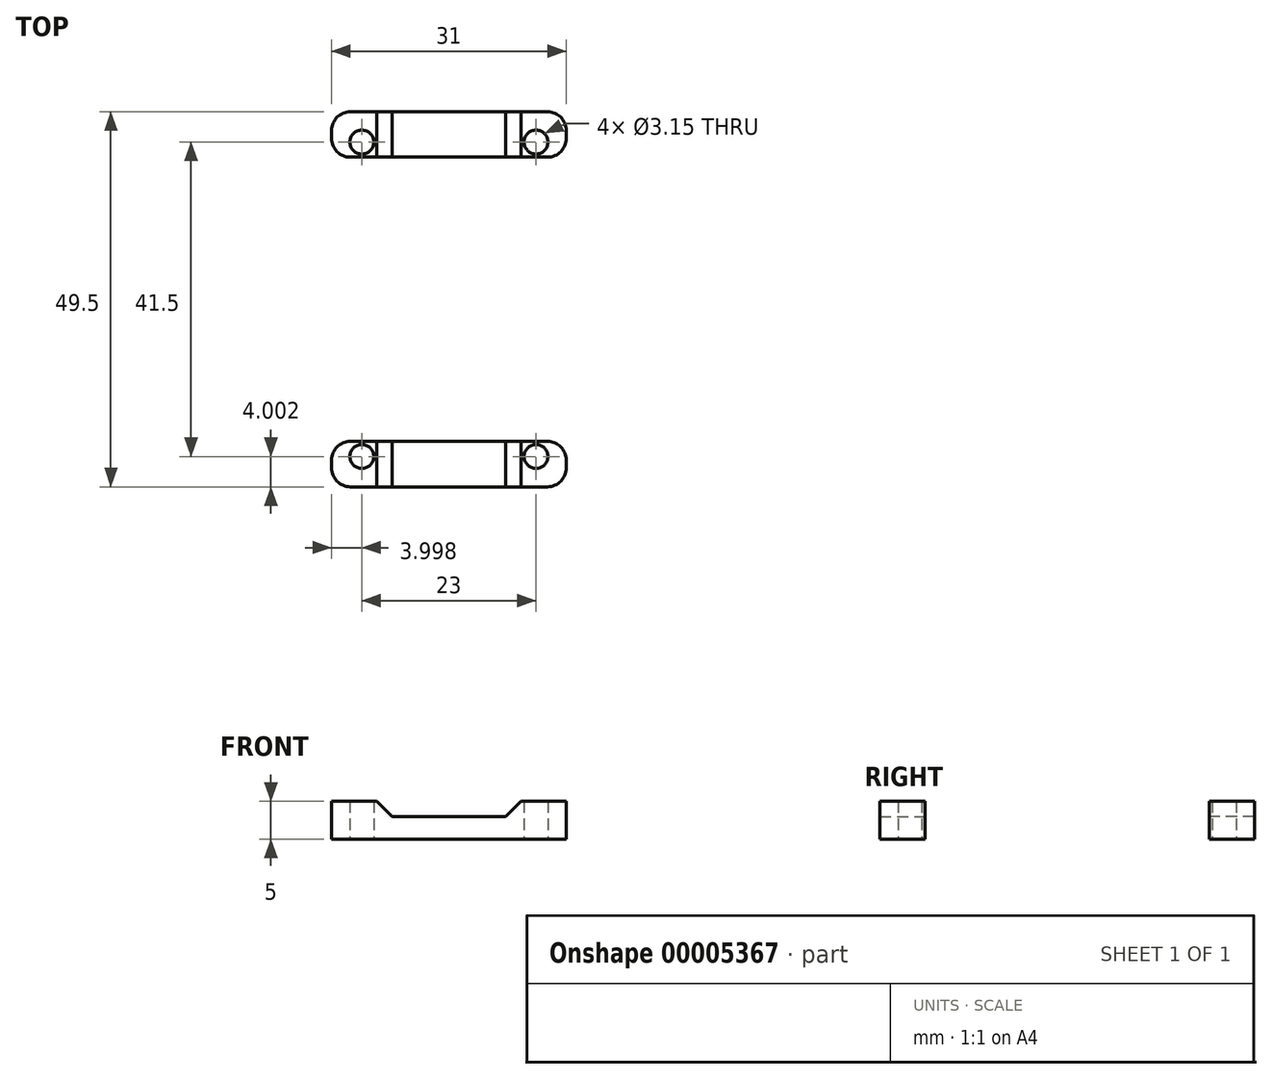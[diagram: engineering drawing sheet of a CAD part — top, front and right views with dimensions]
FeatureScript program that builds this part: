
annotation { "Feature Type Name" : "Feature", "Feature Type Description" : "" }
export const myFeature = defineFeature(function(context is Context, id is Id, definition is map)
    precondition{}
    {
        {
            var Q0;
            Q0=qCreatedBy(makeId("Top.planeOp"),FACE);
            var sketch = newSketch(context, id + "F0", { "sketchPlane" : qUnion([Q0])});
            skCircle(sketch, "E0", {"center": v(-6.84, -9.47) * mm, "radius": 1.57 * mm});
            skCircle(sketch, "E1", {"center": v(16.16, -9.47) * mm, "radius": 1.57 * mm});
            skCircle(sketch, "E2", {"center": v(16.16, 32.03) * mm, "radius": 1.57 * mm});
            skCircle(sketch, "E3", {"center": v(-6.84, 32.03) * mm, "radius": 1.57 * mm});
            skLineSegment(sketch, "E4.bottom", {"start": v(-10.84, 36.03) * mm, "end": v(20.16, 36.03) * mm});
            skLineSegment(sketch, "E4.top", {"start": v(-10.84, -13.47) * mm, "end": v(20.16, -13.47) * mm});
            skLineSegment(sketch, "E4.left", {"start": v(-10.84, 36.03) * mm, "end": v(-10.84, -13.47) * mm});
            skLineSegment(sketch, "E4.right", {"start": v(20.16, 36.03) * mm, "end": v(20.16, -13.47) * mm});
            skLineSegment(sketch, "E5", {"start": v(-4.84, 36.03) * mm, "end": v(-4.84, -13.47) * mm});
            skLineSegment(sketch, "E6", {"start": v(14.16, 36.03) * mm, "end": v(14.16, -13.47) * mm});
            skLineSegment(sketch, "E7", {"start": v(-10.84, 30.03) * mm, "end": v(20.16, 30.03) * mm});
            skLineSegment(sketch, "E8", {"start": v(-10.84, -7.47) * mm, "end": v(20.16, -7.47) * mm});
            skSolve(sketch);
        }
        {
            var Q0;
            Q0=makeQuery(id+"F0.imprint","IMPRINT",FACE,{"disambiguationData":[TD([[makeQuery(id+"F0.imprint","IMPRINT",EDGE,{"derivedFrom":sQuery(id+"F0.wireOp",EDGE,"E0")}),-1.0]])]});
            var Q1;
            Q1=makeQuery(id+"F0.imprint","IMPRINT",FACE,{"disambiguationData":[TD([[makeQuery(id+"F0.imprint","IMPRINT",EDGE,{"derivedFrom":sQuery(id+"F0.wireOp",EDGE,"E1")}),-1.0]])]});
            var Q2;
            Q2=makeQuery(id+"F0.imprint","IMPRINT",FACE,{"disambiguationData":[TD([[makeQuery(id+"F0.imprint","IMPRINT",EDGE,{"derivedFrom":sQuery(id+"F0.wireOp",EDGE,"E2")}),-1.0]])]});
            var Q3;
            Q3=makeQuery(id+"F0.imprint","IMPRINT",FACE,{"disambiguationData":[TD([[makeQuery(id+"F0.imprint","IMPRINT",EDGE,{"derivedFrom":sQuery(id+"F0.wireOp",EDGE,"E3")}),-1.0]])]});
            var Q4;
            {var subQ3=sQuery(id+"F0.wireOp",EDGE,"E5");var subQ5=sQuery(id+"F0.wireOp",EDGE,"E4.bottom");var subQ6=makeQuery(id+"F0.imprint","INTERSECT",VERTEX,{"derivedFrom":[subQ5,subQ3]});Q4=makeQuery(id+"F0.imprint","IMPRINT",FACE,{"disambiguationData":[TD([[makeQuery(id+"F0.imprint","IMPRINT",EDGE,{"disambiguationData":[TD([[subQ6,-1.0]])],"derivedFrom":subQ5}),-1.0]])]});}
            var Q5;
            {var subQ3=sQuery(id+"F0.wireOp",EDGE,"E4.top");var subQ5=sQuery(id+"F0.wireOp",EDGE,"E5");var subQ7=makeQuery(id+"F0.imprint","INTERSECT",VERTEX,{"derivedFrom":[subQ3,subQ5]});Q5=makeQuery(id+"F0.imprint","IMPRINT",FACE,{"disambiguationData":[TD([[makeQuery(id+"F0.imprint","IMPRINT",EDGE,{"disambiguationData":[TD([[subQ7,-1.0]])],"derivedFrom":subQ3}),1.0]])]});}
            extrude(context, id + "F1", {"entities" : qUnion([Q0, Q1, Q2, Q3, Q4, Q5]), "depth" : 3 * mm});
        }
        {
            var Q0;
            Q0=makeQuery(id+"F0.imprint","IMPRINT",FACE,{"disambiguationData":[TD([[makeQuery(id+"F0.imprint","IMPRINT",EDGE,{"derivedFrom":sQuery(id+"F0.wireOp",EDGE,"E3")}),-1.0]])]});
            var Q1;
            Q1=makeQuery(id+"F0.imprint","IMPRINT",FACE,{"disambiguationData":[TD([[makeQuery(id+"F0.imprint","IMPRINT",EDGE,{"derivedFrom":sQuery(id+"F0.wireOp",EDGE,"E2")}),-1.0]])]});
            var Q2;
            Q2=makeQuery(id+"F0.imprint","IMPRINT",FACE,{"disambiguationData":[TD([[makeQuery(id+"F0.imprint","IMPRINT",EDGE,{"derivedFrom":sQuery(id+"F0.wireOp",EDGE,"E1")}),-1.0]])]});
            var Q3;
            Q3=makeQuery(id+"F0.imprint","IMPRINT",FACE,{"disambiguationData":[TD([[makeQuery(id+"F0.imprint","IMPRINT",EDGE,{"derivedFrom":sQuery(id+"F0.wireOp",EDGE,"E0")}),-1.0]])]});
            extrude(context, id + "F2", {"entities" : qUnion([Q0, Q1, Q2, Q3]), "operationType" : NewBodyOperationType.ADD, "depth" : 5 * mm});
        }
        {
            var Q0;
            {var subQ0=sQuery(id+"F0.wireOp",EDGE,"E4.bottom");var subQ1=sQuery(id+"F0.wireOp",EDGE,"E7");var subQ2=sQuery(id+"F0.wireOp",EDGE,"E5");Q0=makeQuery(id+"F2.boolean.opBoolean","INTERSECT",EDGE,{"derivedFrom":[makeQuery(id+"F1.opExtrude","CAP_FACE",FACE,{"disambiguationData":[OSD([sQuery(id+"F0.wireOp",EDGE,"E2"),sQuery(id+"F0.wireOp",EDGE,"E3"),subQ0,sQuery(id+"F0.wireOp",EDGE,"E4.left"),sQuery(id+"F0.wireOp",EDGE,"E4.right"),subQ1])],"isStart":false}),makeQuery(id+"F2.opExtrude","SWEPT_FACE",FACE,{"disambiguationData":[OSD([subQ2]),TDD([makeQuery(id+"F0.imprint","IMPRINT",EDGE,{"disambiguationData":[TD([[makeQuery(id+"F0.imprint","INTERSECT",VERTEX,{"derivedFrom":[subQ0,subQ2]}),-1.0]])],"derivedFrom":subQ2})])]})]});}
            var Q1;
            {var subQ0=sQuery(id+"F0.wireOp",EDGE,"E4.bottom");var subQ1=sQuery(id+"F0.wireOp",EDGE,"E7");var subQ2=sQuery(id+"F0.wireOp",EDGE,"E6");Q1=makeQuery(id+"F2.boolean.opBoolean","INTERSECT",EDGE,{"derivedFrom":[makeQuery(id+"F1.opExtrude","CAP_FACE",FACE,{"disambiguationData":[OSD([sQuery(id+"F0.wireOp",EDGE,"E2"),sQuery(id+"F0.wireOp",EDGE,"E3"),subQ0,sQuery(id+"F0.wireOp",EDGE,"E4.left"),sQuery(id+"F0.wireOp",EDGE,"E4.right"),subQ1])],"isStart":false}),makeQuery(id+"F2.opExtrude","SWEPT_FACE",FACE,{"disambiguationData":[OSD([subQ2]),TDD([makeQuery(id+"F0.imprint","IMPRINT",EDGE,{"disambiguationData":[TD([[makeQuery(id+"F0.imprint","INTERSECT",VERTEX,{"derivedFrom":[subQ0,subQ2]}),-1.0]])],"derivedFrom":subQ2})])]})]});}
            var Q2;
            {var subQ0=sQuery(id+"F0.wireOp",EDGE,"E4.top");var subQ1=sQuery(id+"F0.wireOp",EDGE,"E8");var subQ2=sQuery(id+"F0.wireOp",EDGE,"E6");Q2=makeQuery(id+"F2.boolean.opBoolean","INTERSECT",EDGE,{"derivedFrom":[makeQuery(id+"F1.opExtrude","CAP_FACE",FACE,{"disambiguationData":[OSD([sQuery(id+"F0.wireOp",EDGE,"E0"),sQuery(id+"F0.wireOp",EDGE,"E1"),subQ0,sQuery(id+"F0.wireOp",EDGE,"E4.left"),sQuery(id+"F0.wireOp",EDGE,"E4.right"),subQ1])],"isStart":false}),makeQuery(id+"F2.opExtrude","SWEPT_FACE",FACE,{"disambiguationData":[OSD([subQ2]),TDD([makeQuery(id+"F0.imprint","IMPRINT",EDGE,{"disambiguationData":[TD([[makeQuery(id+"F0.imprint","INTERSECT",VERTEX,{"derivedFrom":[subQ0,subQ2]}),1.0]])],"derivedFrom":subQ2})])]})]});}
            var Q3;
            {var subQ0=sQuery(id+"F0.wireOp",EDGE,"E4.top");var subQ1=sQuery(id+"F0.wireOp",EDGE,"E8");var subQ2=sQuery(id+"F0.wireOp",EDGE,"E5");Q3=makeQuery(id+"F2.boolean.opBoolean","INTERSECT",EDGE,{"derivedFrom":[makeQuery(id+"F1.opExtrude","CAP_FACE",FACE,{"disambiguationData":[OSD([sQuery(id+"F0.wireOp",EDGE,"E0"),sQuery(id+"F0.wireOp",EDGE,"E1"),subQ0,sQuery(id+"F0.wireOp",EDGE,"E4.left"),sQuery(id+"F0.wireOp",EDGE,"E4.right"),subQ1])],"isStart":false}),makeQuery(id+"F2.opExtrude","SWEPT_FACE",FACE,{"disambiguationData":[OSD([subQ2]),TDD([makeQuery(id+"F0.imprint","IMPRINT",EDGE,{"disambiguationData":[TD([[makeQuery(id+"F0.imprint","INTERSECT",VERTEX,{"derivedFrom":[subQ0,subQ2]}),1.0]])],"derivedFrom":subQ2})])]})]});}
            chamfer(context, id + "F3", {"entities" : qUnion([Q0, Q1, Q2, Q3]), "width" : 2 * mm, "tangentPropagation" : true});
        }
        {
            var Q0;
            {var subQ0=sQuery(id+"F0.wireOp",EDGE,"E4.left");var subQ1=sQuery(id+"F0.wireOp",EDGE,"E7");Q0=makeQuery(id+"F2.boolean.opBoolean","MERGE",EDGE,{"derivedFrom":[makeQuery(id+"F1.opExtrude","SWEPT_EDGE",EDGE,{"disambiguationData":[OSD([subQ0,subQ1])]}),makeQuery(id+"F2.opExtrude","SWEPT_EDGE",EDGE,{"disambiguationData":[OSD([subQ0,subQ1])]})]});}
            var Q1;
            {var subQ0=sQuery(id+"F0.wireOp",EDGE,"E4.bottom");var subQ1=sQuery(id+"F0.wireOp",EDGE,"E4.left");Q1=makeQuery(id+"F2.boolean.opBoolean","MERGE",EDGE,{"derivedFrom":[makeQuery(id+"F1.opExtrude","SWEPT_EDGE",EDGE,{"disambiguationData":[OSD([subQ0,subQ1])]}),makeQuery(id+"F2.opExtrude","SWEPT_EDGE",EDGE,{"disambiguationData":[OSD([subQ0,subQ1])]})]});}
            var Q2;
            {var subQ0=sQuery(id+"F0.wireOp",EDGE,"E4.left");var subQ1=sQuery(id+"F0.wireOp",EDGE,"E8");Q2=makeQuery(id+"F2.boolean.opBoolean","MERGE",EDGE,{"derivedFrom":[makeQuery(id+"F1.opExtrude","SWEPT_EDGE",EDGE,{"disambiguationData":[OSD([subQ0,subQ1])]}),makeQuery(id+"F2.opExtrude","SWEPT_EDGE",EDGE,{"disambiguationData":[OSD([subQ0,subQ1])]})]});}
            var Q3;
            {var subQ0=sQuery(id+"F0.wireOp",EDGE,"E4.top");var subQ1=sQuery(id+"F0.wireOp",EDGE,"E4.left");Q3=makeQuery(id+"F2.boolean.opBoolean","MERGE",EDGE,{"derivedFrom":[makeQuery(id+"F1.opExtrude","SWEPT_EDGE",EDGE,{"disambiguationData":[OSD([subQ0,subQ1])]}),makeQuery(id+"F2.opExtrude","SWEPT_EDGE",EDGE,{"disambiguationData":[OSD([subQ0,subQ1])]})]});}
            var Q4;
            {var subQ0=sQuery(id+"F0.wireOp",EDGE,"E4.top");var subQ1=sQuery(id+"F0.wireOp",EDGE,"E4.right");Q4=makeQuery(id+"F2.boolean.opBoolean","MERGE",EDGE,{"derivedFrom":[makeQuery(id+"F1.opExtrude","SWEPT_EDGE",EDGE,{"disambiguationData":[OSD([subQ0,subQ1])]}),makeQuery(id+"F2.opExtrude","SWEPT_EDGE",EDGE,{"disambiguationData":[OSD([subQ0,subQ1])]})]});}
            var Q5;
            {var subQ0=sQuery(id+"F0.wireOp",EDGE,"E4.right");var subQ1=sQuery(id+"F0.wireOp",EDGE,"E8");Q5=makeQuery(id+"F2.boolean.opBoolean","MERGE",EDGE,{"derivedFrom":[makeQuery(id+"F1.opExtrude","SWEPT_EDGE",EDGE,{"disambiguationData":[OSD([subQ0,subQ1])]}),makeQuery(id+"F2.opExtrude","SWEPT_EDGE",EDGE,{"disambiguationData":[OSD([subQ0,subQ1])]})]});}
            var Q6;
            {var subQ0=sQuery(id+"F0.wireOp",EDGE,"E4.right");var subQ1=sQuery(id+"F0.wireOp",EDGE,"E7");Q6=makeQuery(id+"F2.boolean.opBoolean","MERGE",EDGE,{"derivedFrom":[makeQuery(id+"F1.opExtrude","SWEPT_EDGE",EDGE,{"disambiguationData":[OSD([subQ0,subQ1])]}),makeQuery(id+"F2.opExtrude","SWEPT_EDGE",EDGE,{"disambiguationData":[OSD([subQ0,subQ1])]})]});}
            var Q7;
            {var subQ0=sQuery(id+"F0.wireOp",EDGE,"E4.bottom");var subQ1=sQuery(id+"F0.wireOp",EDGE,"E4.right");Q7=makeQuery(id+"F2.boolean.opBoolean","MERGE",EDGE,{"derivedFrom":[makeQuery(id+"F1.opExtrude","SWEPT_EDGE",EDGE,{"disambiguationData":[OSD([subQ0,subQ1])]}),makeQuery(id+"F2.opExtrude","SWEPT_EDGE",EDGE,{"disambiguationData":[OSD([subQ0,subQ1])]})]});}
            fillet(context, id + "F4", {"entities" : qUnion([Q0, Q1, Q2, Q3, Q4, Q5, Q6, Q7]), "radius" : 2.5 * mm, "tangentPropagation" : true, "allowEdgeOverflow" : false});
        }
    });
